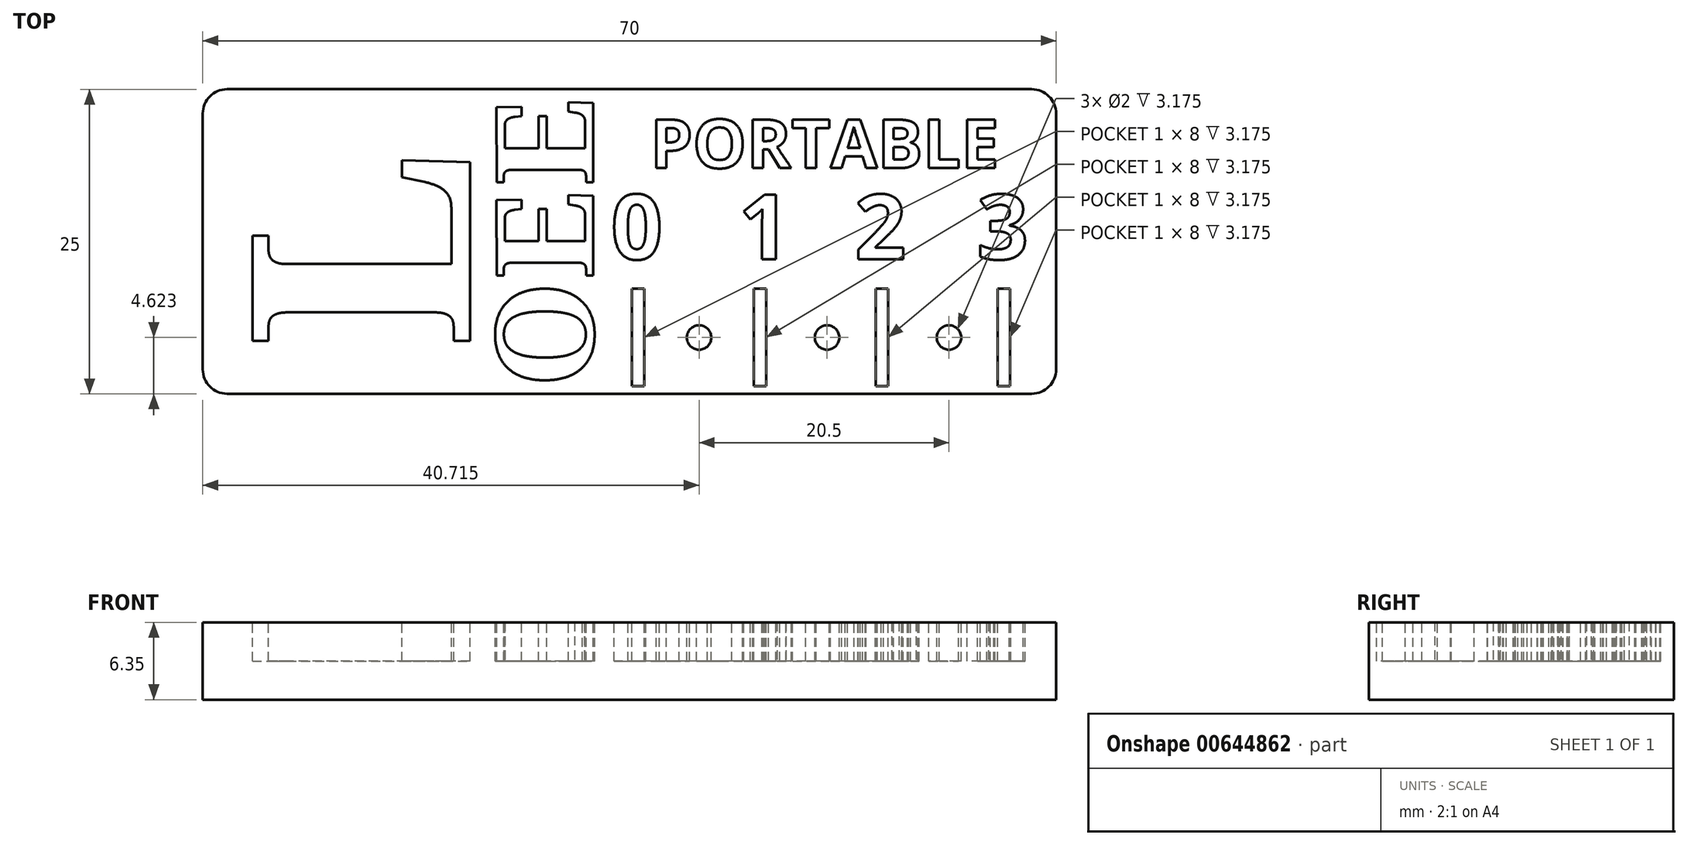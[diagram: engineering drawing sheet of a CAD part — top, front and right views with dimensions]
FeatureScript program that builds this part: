
annotation { "Feature Type Name" : "Feature", "Feature Type Description" : "" }
export const myFeature = defineFeature(function(context is Context, id is Id, definition is map)
    precondition{}
    {
        {
            var Q0;
            Q0=qCreatedBy(makeId("Top.planeOp"),FACE);
            var sketch = newSketch(context, id + "F0", { "sketchPlane" : qUnion([Q0])});
            skLineSegment(sketch, "E0.bottom", {"start": v(-55.27, 9.73) * mm, "end": v(10.73, 9.73) * mm});
            skLineSegment(sketch, "E0.top", {"start": v(-55.27, -15.27) * mm, "end": v(10.73, -15.27) * mm});
            skLineSegment(sketch, "E0.left", {"start": v(-57.27, 7.73) * mm, "end": v(-57.27, -13.27) * mm});
            skLineSegment(sketch, "E0.right", {"start": v(12.73, 7.73) * mm, "end": v(12.73, -13.27) * mm});
            skPoint(sketch, "E1.visualSharp", {"position": v(-57.27, 9.73) * mm});
            skArc(sketch, "E1.filletArc", {"start": v(-55.27, 9.73) * mm, "mid": v(-56.68, 9.15) * mm, "end": v(-57.27, 7.73) * mm});
            skPoint(sketch, "E2.visualSharp", {"position": v(12.73, 9.73) * mm});
            skArc(sketch, "E2.filletArc", {"start": v(12.73, 7.73) * mm, "mid": v(12.14, 9.15) * mm, "end": v(10.73, 9.73) * mm});
            skPoint(sketch, "E3.visualSharp", {"position": v(12.73, -15.27) * mm});
            skArc(sketch, "E3.filletArc", {"start": v(10.73, -15.27) * mm, "mid": v(12.14, -14.68) * mm, "end": v(12.73, -13.27) * mm});
            skPoint(sketch, "E4.visualSharp", {"position": v(-57.27, -15.27) * mm});
            skArc(sketch, "E4.filletArc", {"start": v(-57.27, -13.27) * mm, "mid": v(-56.68, -14.68) * mm, "end": v(-55.27, -15.27) * mm});
            skSolve(sketch);
        }
        {
            var Q0;
            Q0=qSketchRegion(id+"F0",true);
            extrude(context, id + "F1", {"entities" : qUnion([Q0]), "depth" : 6.35 * mm, "offsetDistance" : 25.4 * mm});
        }
        {
            var Q0;
            Q0=makeQuery(id+"F1.opExtrude","CAP_FACE",FACE,{"disambiguationData":[OSD([sQuery(id+"F0.wireOp",EDGE,"E0.bottom"),sQuery(id+"F0.wireOp",EDGE,"E0.top"),sQuery(id+"F0.wireOp",EDGE,"E0.left"),sQuery(id+"F0.wireOp",EDGE,"E0.right")])],"isStart":false});
            var sketch = newSketch(context, id + "F2", { "sketchPlane" : qUnion([Q0])});
            skText(sketch, "E5", { "text": "L", "fontName": "NotoSerif-Bold.ttf"});
            skText(sketch, "E6", { "text": "O\n", "fontName": "NotoSerif-Bold.ttf"});
            skText(sketch, "E7", { "text": "E", "fontName": "NotoSerif-Bold.ttf"});
            skLineSegment(sketch, "E8.bottom", {"start": v(-22.06, -6.65) * mm, "end": v(-21.06, -6.65) * mm});
            skLineSegment(sketch, "E8.top", {"start": v(-22.06, -14.65) * mm, "end": v(-21.06, -14.65) * mm});
            skLineSegment(sketch, "E8.left", {"start": v(-22.06, -6.65) * mm, "end": v(-22.06, -14.65) * mm});
            skLineSegment(sketch, "E8.right", {"start": v(-21.06, -6.65) * mm, "end": v(-21.06, -14.65) * mm});
            skLineSegment(sketch, "E9.bottom", {"start": v(-12.06, -6.65) * mm, "end": v(-11.06, -6.65) * mm});
            skLineSegment(sketch, "E9.top", {"start": v(-12.06, -14.65) * mm, "end": v(-11.06, -14.65) * mm});
            skLineSegment(sketch, "E9.left", {"start": v(-12.06, -6.65) * mm, "end": v(-12.06, -14.65) * mm});
            skLineSegment(sketch, "E9.right", {"start": v(-11.06, -6.65) * mm, "end": v(-11.06, -14.65) * mm});
            skLineSegment(sketch, "E10.bottom", {"start": v(-2.06, -6.65) * mm, "end": v(-1.06, -6.65) * mm});
            skLineSegment(sketch, "E10.top", {"start": v(-2.06, -14.65) * mm, "end": v(-1.06, -14.65) * mm});
            skLineSegment(sketch, "E10.left", {"start": v(-2.06, -6.65) * mm, "end": v(-2.06, -14.65) * mm});
            skLineSegment(sketch, "E10.right", {"start": v(-1.06, -6.65) * mm, "end": v(-1.06, -14.65) * mm});
            skLineSegment(sketch, "E11.bottom", {"start": v(7.94, -6.65) * mm, "end": v(8.94, -6.65) * mm});
            skLineSegment(sketch, "E11.top", {"start": v(7.94, -14.65) * mm, "end": v(8.94, -14.65) * mm});
            skLineSegment(sketch, "E11.left", {"start": v(7.94, -6.65) * mm, "end": v(7.94, -14.65) * mm});
            skLineSegment(sketch, "E11.right", {"start": v(8.94, -6.65) * mm, "end": v(8.94, -14.65) * mm});
            skPoint(sketch, "E12", {"position": v(-21.56, -6.65) * mm});
            skPoint(sketch, "E13", {"position": v(-11.56, -6.65) * mm});
            skPoint(sketch, "E14", {"position": v(-1.56, -6.65) * mm});
            skCircle(sketch, "E15", {"center": v(-16.56, -10.65) * mm, "radius": 1 * mm});
            skPoint(sketch, "E16", {"position": v(-21.06, -10.65) * mm});
            skCircle(sketch, "E17", {"center": v(-6.06, -10.65) * mm, "radius": 1 * mm});
            skCircle(sketch, "E18", {"center": v(3.94, -10.65) * mm, "radius": 1 * mm});
            skPoint(sketch, "E19", {"position": v(-11.06, -10.65) * mm});
            skPoint(sketch, "E20", {"position": v(-1.06, -10.65) * mm});
            skText(sketch, "E21", { "text": "0", "fontName": "OpenSans-Bold.ttf"});
            skText(sketch, "E22", { "text": "1", "fontName": "OpenSans-Bold.ttf"});
            skText(sketch, "E23", { "text": "2", "fontName": "OpenSans-Bold.ttf"});
            skText(sketch, "E24", { "text": "3", "fontName": "OpenSans-Bold.ttf"});
            skLineSegment(sketch, "E25", {"start": v(-39.23, 23.36) * mm, "end": v(-48.9, 23.36) * mm});
            skLineSegment(sketch, "E26", {"start": v(-48.9, 23.36) * mm, "end": v(-48.9, 20.36) * mm});
            skLineSegment(sketch, "E27", {"start": v(-48.9, 20.36) * mm, "end": v(-53.2, 24.99) * mm});
            skLineSegment(sketch, "E28", {"start": v(-53.2, 24.99) * mm, "end": v(-48.9, 28.97) * mm});
            skLineSegment(sketch, "E29", {"start": v(-48.9, 28.97) * mm, "end": v(-48.9, 25.97) * mm});
            skLineSegment(sketch, "E30", {"start": v(-48.9, 25.97) * mm, "end": v(-39.23, 25.97) * mm});
            skPoint(sketch, "E31", {"position": v(-41.72, 24.66) * mm});
            skLineSegment(sketch, "E32", {"start": v(-41.72, 24.66) * mm, "end": v(-39.23, 23.36) * mm});
            skLineSegment(sketch, "E33", {"start": v(-41.72, 24.66) * mm, "end": v(-39.23, 25.97) * mm});
            skText(sketch, "E34", { "text": "E", "fontName": "NotoSerif-Bold.ttf"});
            skText(sketch, "E35", { "text": "PORTABLE", "fontName": "OpenSans-Bold.ttf"});
            const initialGuessF2  = {"E5": [-0.03535, -0.01161, 0, 1, 0.018], "E6": [-0.02523, -0.01477, 0, 1, 0.008], "E7": [-0.02523, -0.00585, -0.00042, 1, 0.008], "E21": [-0.02378, -0.00422, 1, 0, 0.00534], "E22": [-0.01333, -0.00422, 1, 0, 0.00534], "E23": [-0.0038, -0.00422, 1, 0, 0.00534], "E24": [0.00623, -0.00422, 1, 0, 0.00534], "E34": [-0.02523, 0.00178, -0.00042, 1, 0.008], "E35": [-0.02057, 0.00327, 1, 0, 0.004]};
            skSetInitialGuess(sketch, initialGuessF2);
            skSolve(sketch);
        }
        {
            var Q0;
            Q0=qSketchRegion(id+"F2",true);
            extrude(context, id + "F3", {"entities" : qUnion([Q0]), "operationType" : NewBodyOperationType.REMOVE, "oppositeDirection" : true, "depth" : 3.17 * mm, "offsetDistance" : 25.4 * mm});
        }
    });
